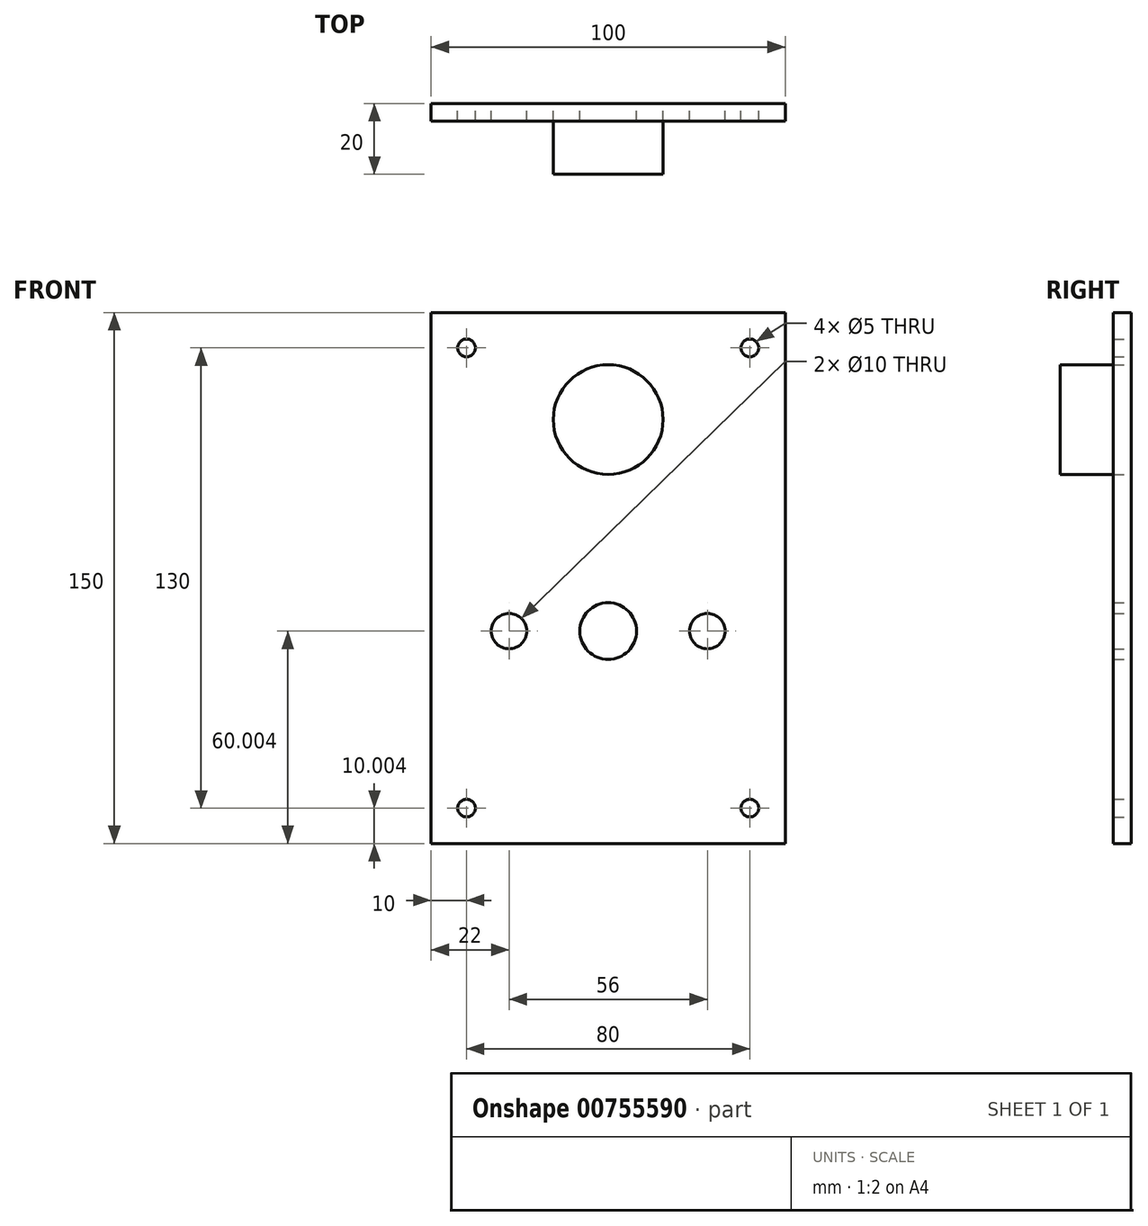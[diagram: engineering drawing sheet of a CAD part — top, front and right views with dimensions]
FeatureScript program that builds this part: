
annotation { "Feature Type Name" : "Feature", "Feature Type Description" : "" }
export const myFeature = defineFeature(function(context is Context, id is Id, definition is map)
    precondition{}
    {
        {
            var Q0;
            Q0=qCreatedBy(makeId("Front.planeOp"),FACE);
            var sketch = newSketch(context, id + "F0", { "sketchPlane" : qUnion([Q0])});
            skLineSegment(sketch, "E0.bottom", {"start": v(-50, 69.44) * mm, "end": v(50, 69.44) * mm});
            skLineSegment(sketch, "E0.top", {"start": v(-50, -80.56) * mm, "end": v(50, -80.56) * mm});
            skLineSegment(sketch, "E0.left", {"start": v(-50, 69.44) * mm, "end": v(-50, -80.56) * mm});
            skLineSegment(sketch, "E0.right", {"start": v(50, 69.44) * mm, "end": v(50, -80.56) * mm});
            skCircle(sketch, "E1", {"center": v(0, -20.56) * mm, "radius": 8 * mm});
            skCircle(sketch, "E2", {"center": v(-40, 59.44) * mm, "radius": 2.5 * mm});
            skCircle(sketch, "E3", {"center": v(40, 59.44) * mm, "radius": 2.5 * mm});
            skCircle(sketch, "E4", {"center": v(-40, -70.56) * mm, "radius": 2.5 * mm});
            skCircle(sketch, "E5", {"center": v(40, -70.56) * mm, "radius": 2.5 * mm});
            skCircle(sketch, "E6", {"center": v(-28, -20.56) * mm, "radius": 2.5 * mm});
            skCircle(sketch, "E7", {"center": v(28, -20.56) * mm, "radius": 2.5 * mm});
            skCircle(sketch, "E8", {"center": v(-28, -20.56) * mm, "radius": 5 * mm});
            skCircle(sketch, "E9", {"center": v(28, -20.56) * mm, "radius": 5 * mm});
            skSolve(sketch);
        }
        {
            var Q0;
            Q0=makeQuery(id+"F0.imprint","IMPRINT",FACE,{"disambiguationData":[TD([[makeQuery(id+"F0.imprint","IMPRINT",EDGE,{"derivedFrom":sQuery(id+"F0.wireOp",EDGE,"E0.bottom")}),-1.0]])]});
            extrude(context, id + "F1", {"entities" : qUnion([Q0]), "depth" : 5 * mm, "offsetDistance" : 25 * mm});
        }
        {
            var Q0;
            Q0=qCreatedBy(makeId("Front.planeOp"),FACE);
            var sketch = newSketch(context, id + "F2", { "sketchPlane" : qUnion([Q0])});
            skCircle(sketch, "E10", {"center": v(0, 39.18) * mm, "radius": 15.5 * mm});
            skSolve(sketch);
        }
        {
            var Q0;
            Q0 = qSketchRegion(id + "F2", true);
            extrude(context, id + "F3", {"entities" : qUnion([Q0]), "depth" : 20 * mm, "offsetDistance" : 25 * mm});
        }
    });
